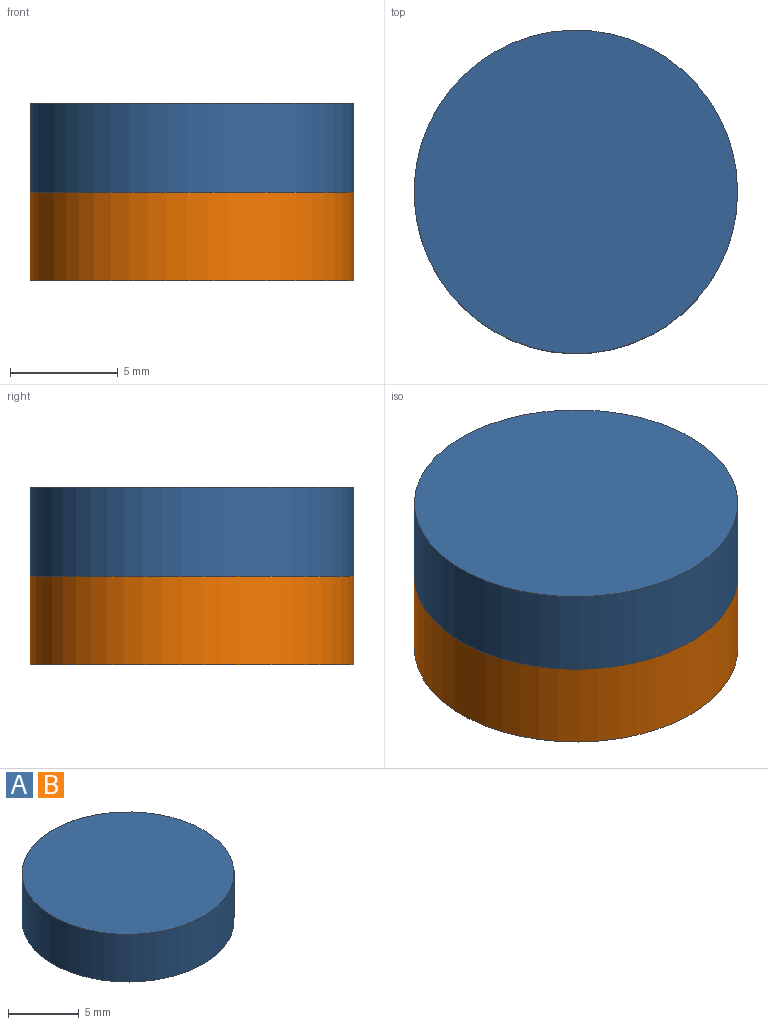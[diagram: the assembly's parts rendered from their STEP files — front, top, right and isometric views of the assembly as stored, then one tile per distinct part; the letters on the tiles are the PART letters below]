
ASSEMBLY  parts=2 mates=1
PART A: 3 faces, bbox 15x15x4.1 mm
  f0: cylinder r=7.5mm len=15mm, axis (0,0,-1), area 194.4mm2, adj f1,f2
  f1: plane 15x15mm, normal (0,0,1), area 176.7mm2, adj f0
  f2: plane 15x15mm, normal (0,0,-1), area 176.7mm2, adj f0
PART B: same geometry as A
PLACE A rot(axis=(1,0,0),180deg) t=(11.75,-1.73,7.9)mm
PLACE B t=(11.75,-1.73,-0.35)mm
MATE fastened A.f0 <-> B.f0  axis (0,0,-1) through (11.75,-1.73,3.77)mm
